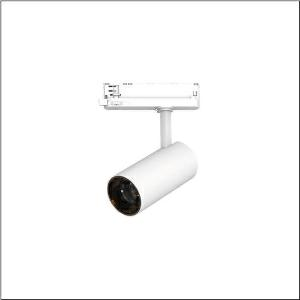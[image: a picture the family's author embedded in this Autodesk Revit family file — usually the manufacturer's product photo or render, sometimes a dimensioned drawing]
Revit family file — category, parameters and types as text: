
# Revit family: spot_31_slim_51sf127fb2b
name_source: partatom
category: Lighting Fixtures
units: mm (PartAtom-declared; Revit-internal decimal feet)

## family parameters
Cut with Voids When Loaded = No
Host = Face
Light Source = No
Part Type = Normal
Room Calculation Point = No
Round Connector Dimension = Use Diameter
Shared = No

## types (1)
- Spot 31 Slim (1 x LED, 1970 lm, 16.2 W, 3000K)
    Apparent Load = 16 VA
    CIE Flux Codes = 94 98 99 100 100
    Color Rendering = 90
    Color Temperature = 3000K
    Default Elevation = 1800 mm
    Description = Spot 31 Slim, directional spotlight, light control with reflector, of aluminium, LED rated luminous flux: 2.150lm, light colour: 930, control gear: ECG, with 3-phase adapter, mains connection: 220..240V, AC, 50/60Hz, housing, of aluminium, traffic white (RAL 9016), diameter: 70mm, adapter, of plastic, protection rating (complete): IP20, insulation class (complete): insulation class I (protective earthing), certification: CE, impact resistance: IK02, packaging unit: 1 piece
    Height = 210 mm
    Lamp = 1 x LED
    Lamp Light Flux = 1970 lm
    Lamp Power = 16.2 W
    Lamp count = 1
    Length = 70 mm
    Luminous efficacy = 122 lm/W
    Manufacturer = Siteco
    ModVariant = No
    Model = 51SF127FB2B
    Mounting Place = Ceiling
    Mounting Type = Pendant
    Number of Poles = 1
    OnlyDefault = Yes
    Power Factor = 1
    Product Name = Spot 31 Slim
    Product group = directional spotlight
    ProductGroupID = 905
    Protection Class = Protection class I
    Protection Degree = IP 20
    RLX_Detail_Level = 1
    RLX_Emergency_Light_Flux = 0 lm
    RLX_Emergency_Type = 0
    RLX_Emergency_Type_DB = No
    RlxData = <blob elided: 14173 chars, md5=a547fd4a>
    Socket = socket
    Standby Power = 0 W
    System Light Flux = 1970 lm
    System Power = 16 W
    Type Comments = Product without accessories
    Type Image = l_1228468.jpg
    URL = http://relux.com
    VarID = ---
    Voltage = 0 V
    Weight = 0.00 kg
    Width = 0 mm  [stored 0 ft]

note: [stored X ft] marks values corroborated as IEEE doubles in the binary element streams (Revit-internal decimal feet)

## geometry (parser evidence)
native form markers: Sweep x12
no freeform markers — native parametric forms only
